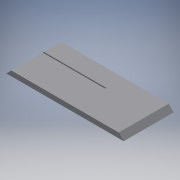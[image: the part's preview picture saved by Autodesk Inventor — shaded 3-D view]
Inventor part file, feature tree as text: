
AUTODESK INVENTOR PART (.ipt)
format: ipt  version: 2018.3 (Build 223284000, 284)  size: 243,200 bytes
history: native  units: mm
features: extrude x6, sketch x6
ambient origin geometry x8: Origin, YZ Plane, XZ Plane, XY Plane, X Axis, Y Axis, Z Axis, Center Point
bodies: Solid1 (feature_tree)
feature tree (12):
  extrude  "Extrusion1"  Depth=20.0mm
  extrude  "Extrusion2"  Depth=2.0mm
  extrude  "Extrusion5"  Depth=20.0mm TaperAngle=0.0deg
  extrude  "Extrusion6"  Depth=10.0mm
  extrude  "Extrusion7"  Depth=5.0mm
  extrude  "Extrusion8"  Depth=1.5mm TaperAngle=0.0deg
  sketch  "Sketch1"  dims[d0=43.0mm d1=20.0mm]
  sketch  "Sketch2"  dims[d2=2.0mm d3=0.0mm d4=2.0mm]
  sketch  "Sketch5"  dims[d5=2.0mm d6=20.0mm d7=0.0mm]
  sketch  "Sketch6"  dims[d26=20.0mm d27=10.0mm]
  sketch  "Sketch7"  dims[d28=5.0mm d29=5.0mm]
  sketch  "Sketch8"  dims[d30=5.0mm d31=1.5mm d32=0.0mm d33=1.5mm d34=0.0mm d35=0.5mm d36=2.0mm d37=0.0mm d38=25.0mm d39=0.5mm d40=2.0mm d41=0.0mm]
